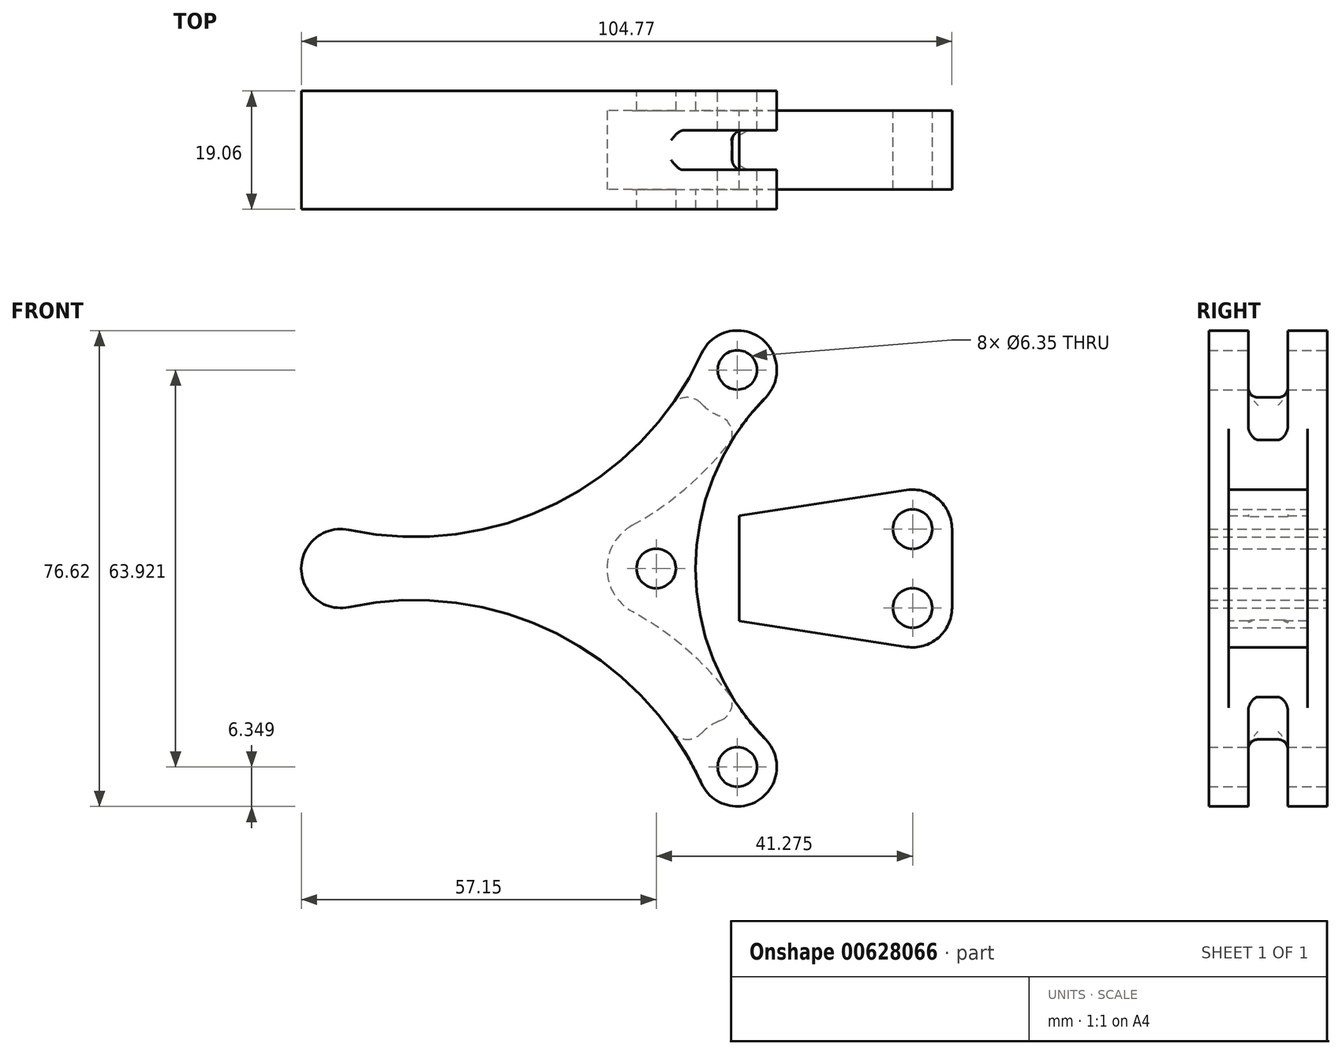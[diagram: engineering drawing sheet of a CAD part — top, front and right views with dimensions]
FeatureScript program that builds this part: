
annotation { "Feature Type Name" : "Feature", "Feature Type Description" : "" }
export const myFeature = defineFeature(function(context is Context, id is Id, definition is map)
    precondition{}
    {
        {
            var Q0;
            Q0=qCreatedBy(makeId("Front.planeOp"),FACE);
            var sketch = newSketch(context, id + "F0", { "sketchPlane" : qUnion([Q0])});
            skArc(sketch, "E0", {"start": v(34.93, 6.35) * mm, "mid": v(32.7, 11.17) * mm, "end": v(27.6, 12.63) * mm});
            skArc(sketch, "E1", {"start": v(27.6, -12.63) * mm, "mid": v(32.7, -11.17) * mm, "end": v(34.93, -6.35) * mm});
            skArc(sketch, "E2", {"start": v(-13.67, 6.28) * mm, "mid": v(-19.05, 0) * mm, "end": v(-13.67, -6.28) * mm});
            skLineSegment(sketch, "E3", {"start": v(27.6, 12.63) * mm, "end": v(-13.67, 6.28) * mm});
            skLineSegment(sketch, "E4", {"start": v(-13.67, -6.28) * mm, "end": v(27.6, -12.63) * mm});
            skLineSegment(sketch, "E5", {"start": v(34.93, -6.35) * mm, "end": v(34.93, 6.35) * mm});
            skPoint(sketch, "E6", {"position": v(34.93, 0) * mm});
            skCircle(sketch, "E7", {"center": v(-12.7, 0) * mm, "radius": 3.18 * mm});
            skCircle(sketch, "E8", {"center": v(28.58, 6.35) * mm, "radius": 3.18 * mm});
            skCircle(sketch, "E9", {"center": v(28.58, -6.35) * mm, "radius": 3.18 * mm});
            skSolve(sketch);
        }
        {
            var Q0;
            Q0=makeQuery(id+"F0.imprint","IMPRINT",FACE,{"disambiguationData":[TD([[makeQuery(id+"F0.imprint","IMPRINT",EDGE,{"derivedFrom":sQuery(id+"F0.wireOp",EDGE,"E0")}),1.0]])]});
            extrude(context, id + "F1", {"entities" : qUnion([Q0]), "endBound" : BoundingType.SYMMETRIC, "depth" : 12.7 * mm, "offsetDistance" : 25.4 * mm});
        }
        {
            var Q0;
            Q0=qCreatedBy(makeId("Front.planeOp"),FACE);
            var sketch = newSketch(context, id + "F2", { "sketchPlane" : qUnion([Q0])});
            skLineSegment(sketch, "E10.0", {"start": v(27.6, 12.63) * mm, "end": v(-13.67, 6.28) * mm});
            skLineSegment(sketch, "E11.0", {"start": v(-13.67, -6.28) * mm, "end": v(27.6, -12.63) * mm});
            skArc(sketch, "E12", {"start": v(-6.65, -7.36) * mm, "mid": v(-3.17, 0) * mm, "end": v(-6.65, 7.36) * mm, "construction": true});
            skArc(sketch, "E13", {"start": v(2.02, 8.7) * mm, "mid": v(-2.13, 6.17) * mm, "end": v(-3.29, 1.45) * mm});
            skArc(sketch, "E14", {"start": v(-3.29, -1.45) * mm, "mid": v(-2.13, -6.17) * mm, "end": v(2.02, -8.7) * mm});
            skArc(sketch, "E15", {"start": v(-3.29, -1.45) * mm, "mid": v(-3.18, 0) * mm, "end": v(-3.29, 1.45) * mm});
            skLineSegment(sketch, "E16", {"start": v(2.02, 8.7) * mm, "end": v(-19.05, 8.7) * mm});
            skLineSegment(sketch, "E17", {"start": v(-19.05, 8.7) * mm, "end": v(-19.05, -8.7) * mm});
            skLineSegment(sketch, "E18", {"start": v(-19.05, -8.7) * mm, "end": v(2.02, -8.7) * mm});
            skSolve(sketch);
        }
        {
            var Q0;
            Q0=makeQuery(id+"F2.imprint","IMPRINT",FACE,{"disambiguationData":[TD([[makeQuery(id+"F2.imprint","IMPRINT",EDGE,{"derivedFrom":sQuery(id+"F2.wireOp",EDGE,"E13")}),-1.0]])]});
            extrude(context, id + "F3", {"entities" : qUnion([Q0]), "operationType" : NewBodyOperationType.REMOVE, "endBound" : BoundingType.SYMMETRIC, "oppositeDirection" : true, "depth" : 6.35 * mm, "offsetDistance" : 25.4 * mm});
        }
        {
            var Q0;
            Q0=qCreatedBy(makeId("Front.planeOp"),FACE);
            var sketch = newSketch(context, id + "F4", { "sketchPlane" : qUnion([Q0])});
            skCircle(sketch, "E19.0", {"center": v(-12.7, 0) * mm, "radius": 3.18 * mm});
            skCircle(sketch, "E20", {"center": v(-12.7, 0) * mm, "radius": 6.35 * mm});
            skArc(sketch, "E21", {"start": v(4.9, 27.51) * mm, "mid": v(-6.35, 0) * mm, "end": v(4.9, -27.51) * mm});
            skArc(sketch, "E22", {"start": v(4.9, 27.51) * mm, "mid": v(3.97, 37.19) * mm, "end": v(-5.4, 34.62) * mm});
            skLineSegment(sketch, "E23", {"start": v(-12.7, 0) * mm, "end": v(0.37, 31.96) * mm, "construction": true});
            skLineSegment(sketch, "E24", {"start": v(-12.7, 0) * mm, "end": v(0.37, -31.96) * mm, "construction": true});
            skLineSegment(sketch, "E25", {"start": v(-12.7, 0) * mm, "end": v(-63.5, 0) * mm, "construction": true});
            skArc(sketch, "E26", {"start": v(-62.17, 6.2) * mm, "mid": v(-69.85, 0) * mm, "end": v(-62.17, -6.2) * mm});
            skArc(sketch, "E27", {"start": v(-62.17, 6.2) * mm, "mid": v(-28.8, 10.45) * mm, "end": v(-5.4, 34.62) * mm});
            skArc(sketch, "E28", {"start": v(-5.4, -34.62) * mm, "mid": v(-28.8, -10.45) * mm, "end": v(-62.17, -6.2) * mm});
            skLineSegment(sketch, "E29", {"start": v(0.37, 31.96) * mm, "end": v(28.57, 6.35) * mm, "construction": true});
            skLineSegment(sketch, "E30", {"start": v(0.37, -31.96) * mm, "end": v(28.58, -6.35) * mm, "construction": true});
            skCircle(sketch, "E31", {"center": v(0.37, 31.96) * mm, "radius": 3.18 * mm});
            skCircle(sketch, "E32", {"center": v(0.37, -31.96) * mm, "radius": 3.18 * mm});
            skArc(sketch, "E33", {"start": v(-5.4, -34.62) * mm, "mid": v(3.97, -37.19) * mm, "end": v(4.9, -27.51) * mm});
            skSolve(sketch);
        }
        {
            var Q0;
            Q0=makeQuery(id+"F4.imprint","IMPRINT",FACE,{"disambiguationData":[TD([[makeQuery(id+"F4.imprint","IMPRINT",EDGE,{"derivedFrom":sQuery(id+"F4.wireOp",EDGE,"E19.0")}),-1.0]])]});
            var Q1;
            {var subQ3=sQuery(id+"F4.wireOp",EDGE,"E20");Q1=makeQuery(id+"F4.imprint","IMPRINT",FACE,{"disambiguationData":[TD([[makeQuery(id+"F4.imprint","IMPRINT",EDGE,{"derivedFrom":subQ3}),-1.0]])]});}
            extrude(context, id + "F5", {"entities" : qUnion([Q0, Q1]), "endBound" : BoundingType.SYMMETRIC, "depth" : 19.05 * mm, "offsetDistance" : 25.4 * mm});
        }
        {
            var Q0;
            Q0=qCreatedBy(makeId("Front.planeOp"),FACE);
            var sketch = newSketch(context, id + "F6", { "sketchPlane" : qUnion([Q0])});
            skArc(sketch, "E34.0", {"start": v(4.9, 27.51) * mm, "mid": v(2.69, 25.07) * mm, "end": v(0.7, 22.44) * mm, "construction": true});
            skCircle(sketch, "E35", {"center": v(0.37, 31.96) * mm, "radius": 7.94 * mm});
            skCircle(sketch, "E36", {"center": v(0.37, -31.96) * mm, "radius": 7.94 * mm});
            skArc(sketch, "E37", {"start": v(-16.52, 6.96) * mm, "mid": v(-20.64, 0) * mm, "end": v(-16.52, -6.96) * mm});
            skArc(sketch, "E38", {"start": v(-16.52, 6.96) * mm, "mid": v(-7.02, 13.7) * mm, "end": v(0.7, 22.44) * mm});
            skArc(sketch, "E39", {"start": v(0.7, -22.44) * mm, "mid": v(-7.02, -13.7) * mm, "end": v(-16.52, -6.96) * mm});
            skArc(sketch, "E40.trimOffspring", {"start": v(0.7, -22.44) * mm, "mid": v(2.69, -25.07) * mm, "end": v(4.9, -27.51) * mm, "construction": true});
            skLineSegment(sketch, "E41", {"start": v(0.7, 22.44) * mm, "end": v(0.7, -22.44) * mm});
            skSolve(sketch);
        }
        {
            var Q0;
            Q0=makeQuery(id+"F6.imprint","IMPRINT",FACE,{"disambiguationData":[TD([[makeQuery(id+"F6.imprint","IMPRINT",EDGE,{"derivedFrom":sQuery(id+"F6.wireOp",EDGE,"E37")}),1.0]])]});
            extrude(context, id + "F7", {"entities" : qUnion([Q0]), "operationType" : NewBodyOperationType.REMOVE, "endBound" : BoundingType.SYMMETRIC, "oppositeDirection" : true, "depth" : 12.7 * mm, "offsetDistance" : 25.4 * mm});
        }
        {
            var Q0;
            Q0=makeQuery(id+"F6.imprint","IMPRINT",FACE,{"disambiguationData":[TD([[makeQuery(id+"F6.imprint","IMPRINT",EDGE,{"derivedFrom":sQuery(id+"F6.wireOp",EDGE,"E35")}),1.0]])]});
            var Q1;
            Q1=makeQuery(id+"F6.imprint","IMPRINT",FACE,{"disambiguationData":[TD([[makeQuery(id+"F6.imprint","IMPRINT",EDGE,{"derivedFrom":sQuery(id+"F6.wireOp",EDGE,"E36")}),1.0]])]});
            extrude(context, id + "F8", {"entities" : qUnion([Q0, Q1]), "operationType" : NewBodyOperationType.REMOVE, "endBound" : BoundingType.SYMMETRIC, "oppositeDirection" : true, "depth" : 6.35 * mm, "offsetDistance" : 25.4 * mm});
        }
        {
            var Q0;
            Q0=makeQuery(id+"F8.boolean.opBoolean","INTERSECT",EDGE,{"derivedFrom":[makeQuery(id+"F5.opExtrude","SWEPT_FACE",FACE,{"disambiguationData":[OSD([sQuery(id+"F4.wireOp",EDGE,"E21")])]}),makeQuery(id+"F8.opExtrude","SWEPT_FACE",FACE,{"disambiguationData":[OSD([sQuery(id+"F6.wireOp",EDGE,"E35")])]})]});
            var Q1;
            Q1=makeQuery(id+"F8.boolean.opBoolean","INTERSECT",EDGE,{"derivedFrom":[makeQuery(id+"F5.opExtrude","SWEPT_FACE",FACE,{"disambiguationData":[OSD([sQuery(id+"F4.wireOp",EDGE,"E27")])]}),makeQuery(id+"F8.opExtrude","SWEPT_FACE",FACE,{"disambiguationData":[OSD([sQuery(id+"F6.wireOp",EDGE,"E35")])]})]});
            var Q2;
            Q2=makeQuery(id+"F8.boolean.opBoolean","INTERSECT",EDGE,{"derivedFrom":[makeQuery(id+"F5.opExtrude","SWEPT_FACE",FACE,{"disambiguationData":[OSD([sQuery(id+"F4.wireOp",EDGE,"E28")])]}),makeQuery(id+"F8.opExtrude","SWEPT_FACE",FACE,{"disambiguationData":[OSD([sQuery(id+"F6.wireOp",EDGE,"E36")])]})]});
            var Q3;
            Q3=makeQuery(id+"F8.boolean.opBoolean","INTERSECT",EDGE,{"derivedFrom":[makeQuery(id+"F5.opExtrude","SWEPT_FACE",FACE,{"disambiguationData":[OSD([sQuery(id+"F4.wireOp",EDGE,"E21")])]}),makeQuery(id+"F8.opExtrude","SWEPT_FACE",FACE,{"disambiguationData":[OSD([sQuery(id+"F6.wireOp",EDGE,"E36")])]})]});
            fillet(context, id + "F9", {"entities" : qUnion([Q0, Q1, Q2, Q3]), "radius" : 3.17 * mm, "tangentPropagation" : true, "allowEdgeOverflow" : false});
        }
        {
            var Q0;
            Q0=makeQuery(id+"F8.boolean.opBoolean","COPY",EDGE,{"derivedFrom":makeQuery(id+"F8.opExtrude","CAP_EDGE",EDGE,{"disambiguationData":[OSD([sQuery(id+"F6.wireOp",EDGE,"E35")])],"isStart":false})});
            var Q1;
            Q1=makeQuery(id+"F8.boolean.opBoolean","COPY",EDGE,{"derivedFrom":makeQuery(id+"F8.opExtrude","CAP_EDGE",EDGE,{"disambiguationData":[OSD([sQuery(id+"F6.wireOp",EDGE,"E35")])],"isStart":true})});
            var Q2;
            Q2=makeQuery(id+"F8.boolean.opBoolean","COPY",EDGE,{"derivedFrom":makeQuery(id+"F8.opExtrude","CAP_EDGE",EDGE,{"disambiguationData":[OSD([sQuery(id+"F6.wireOp",EDGE,"E36")])],"isStart":false})});
            var Q3;
            Q3=makeQuery(id+"F8.boolean.opBoolean","COPY",EDGE,{"derivedFrom":makeQuery(id+"F8.opExtrude","CAP_EDGE",EDGE,{"disambiguationData":[OSD([sQuery(id+"F6.wireOp",EDGE,"E36")])],"isStart":true})});
            fillet(context, id + "F10", {"entities" : qUnion([Q0, Q1, Q2, Q3]), "radius" : 1.59 * mm, "tangentPropagation" : true, "allowEdgeOverflow" : false});
        }
        {
            var Q0;
            Q0=makeQuery(id+"F3.boolean.opBoolean","COPY",EDGE,{"derivedFrom":makeQuery(id+"F3.opExtrude","CAP_EDGE",EDGE,{"disambiguationData":[OSD([sQuery(id+"F2.wireOp",EDGE,"E14")])],"isStart":true})});
            var Q1;
            Q1=makeQuery(id+"F3.boolean.opBoolean","COPY",EDGE,{"derivedFrom":makeQuery(id+"F3.opExtrude","CAP_EDGE",EDGE,{"disambiguationData":[OSD([sQuery(id+"F2.wireOp",EDGE,"E14")])],"isStart":false})});
            fillet(context, id + "F11", {"entities" : qUnion([Q0, Q1]), "radius" : 1.59 * mm, "tangentPropagation" : true, "allowEdgeOverflow" : false});
        }
    });
